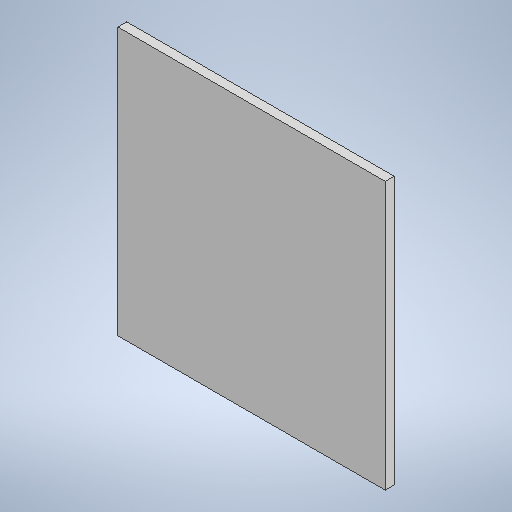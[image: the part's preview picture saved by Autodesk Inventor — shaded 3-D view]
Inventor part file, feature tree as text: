
AUTODESK INVENTOR PART (.ipt)
format: ipt  version: 2025.1 (Build 291241020, 241B)  size: 226,304 bytes
history: native  units: in
note: dims shown in document units (in); Inventor stores cm internally (conversion verified against a paired STEP export)
features: extrude x1, sketch x1
ambient origin geometry x8: Origin, YZ Plane, XZ Plane, XY Plane, X Axis, Y Axis, Z Axis, Center Point
bodies: Solid1 (feature_tree)
feature tree (2):
  extrude  "Extrusion1"  [1 undecoded]
  sketch  "Sketch1"  dims[d27=0.2in d28=0.0in]
note: 1 required parameter value undecoded (feature->parameter linkage not recoverable at this tier; creation-order binding heuristic only, values carry confidence <= 0.55)
